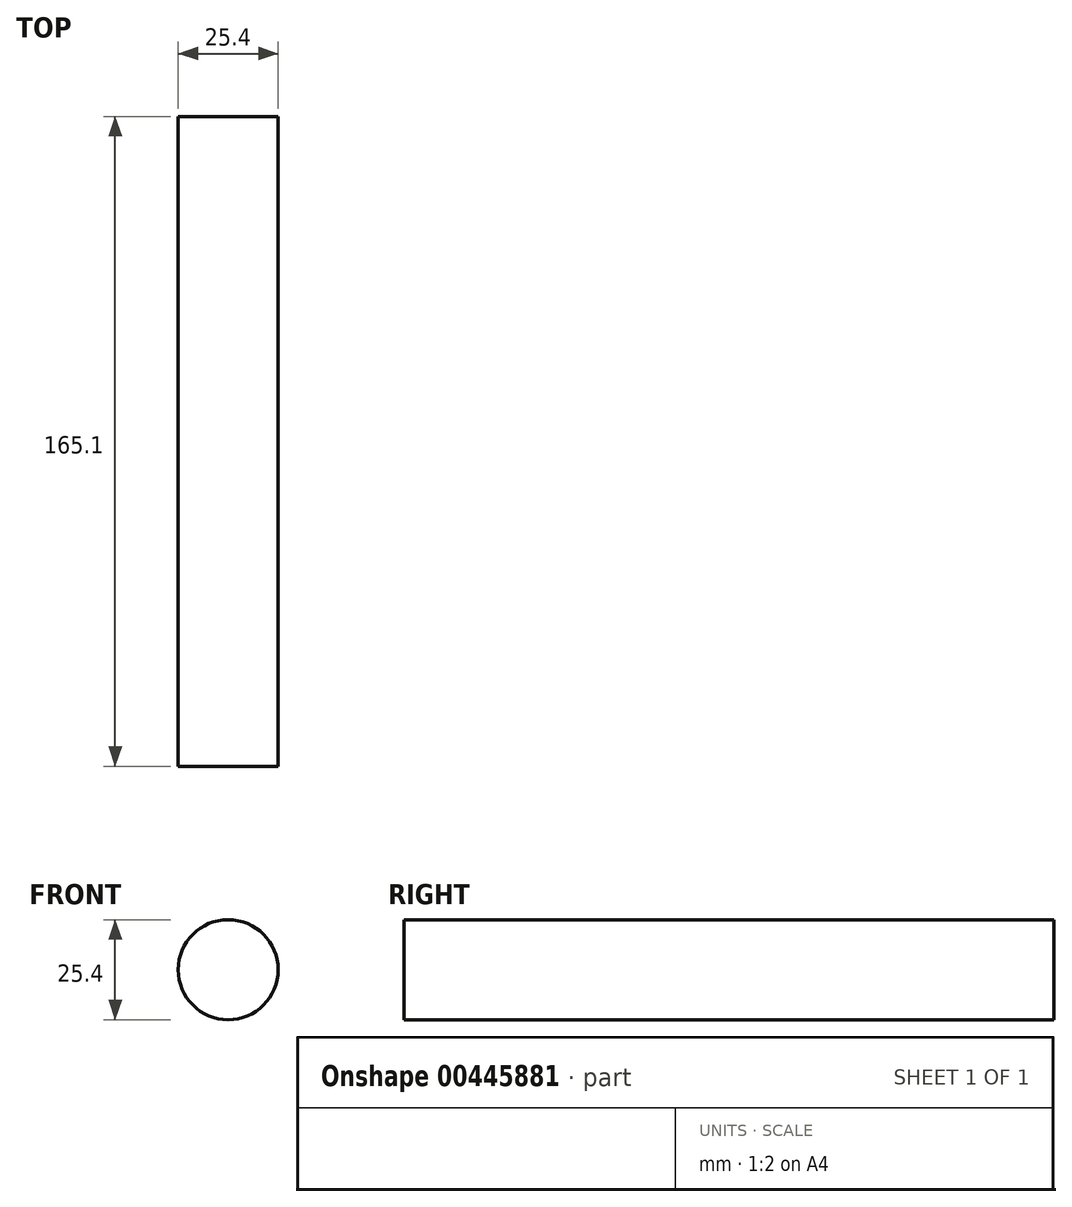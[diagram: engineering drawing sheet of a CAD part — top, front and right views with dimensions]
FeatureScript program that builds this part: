
annotation { "Feature Type Name" : "Feature", "Feature Type Description" : "" }
export const myFeature = defineFeature(function(context is Context, id is Id, definition is map)
    precondition{}
    {
        {
            var Q0;
            Q0=qCreatedBy(makeId("Front.planeOp"),FACE);
            var sketch = newSketch(context, id + "F0", { "sketchPlane" : qUnion([Q0])});
            skCircle(sketch, "E0", {"center": v(0, 0) * mm, "radius": 12.7 * mm});
            skSolve(sketch);
        }
        {
            var Q0;
            Q0=makeQuery(id+"F0.imprint","IMPRINT",FACE,{"disambiguationData":[TD([[makeQuery(id+"F0.imprint","IMPRINT",EDGE,{"derivedFrom":sQuery(id+"F0.wireOp",EDGE,"E0")}),1.0]])]});
            extrude(context, id + "F1", {"entities" : qUnion([Q0]), "depth" : 165.1 * mm});
        }
    });
